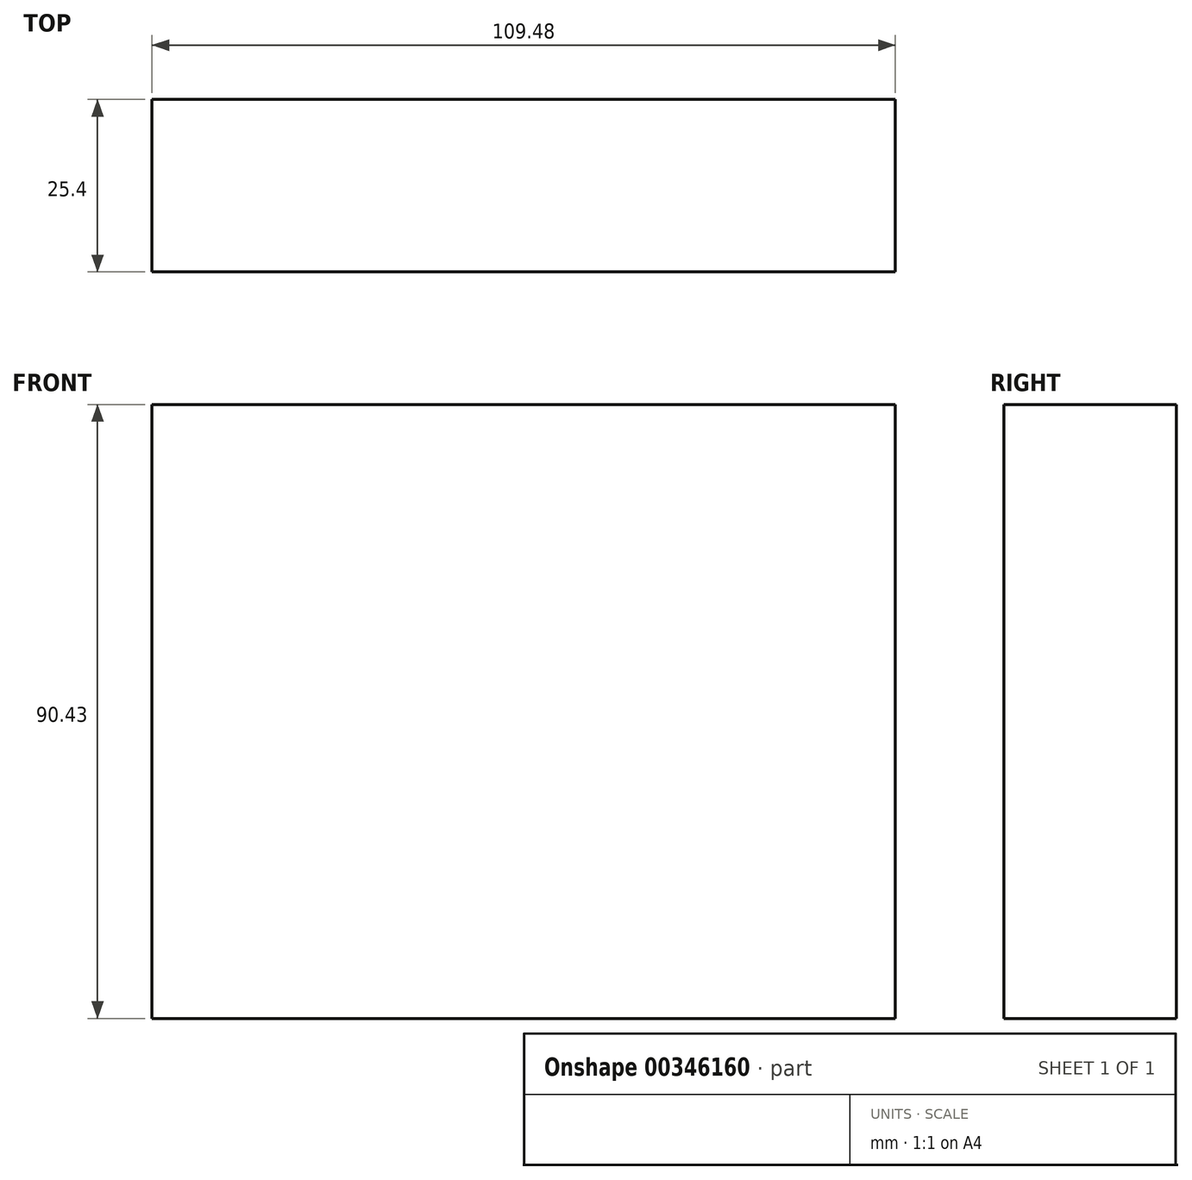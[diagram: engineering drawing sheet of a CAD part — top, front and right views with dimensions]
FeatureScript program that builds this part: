
annotation { "Feature Type Name" : "Feature", "Feature Type Description" : "" }
export const myFeature = defineFeature(function(context is Context, id is Id, definition is map)
    precondition{}
    {
        {
            var Q0;
            Q0=qCreatedBy(makeId("Front.planeOp"),FACE);
            var sketch = newSketch(context, id + "F0", { "sketchPlane" : qUnion([Q0])});
            skLineSegment(sketch, "E0", {"start": v(-49.86, 38.8) * mm, "end": v(-49.86, -51.62) * mm});
            skLineSegment(sketch, "E1", {"start": v(-49.86, -51.62) * mm, "end": v(59.62, -51.62) * mm});
            skLineSegment(sketch, "E2", {"start": v(59.62, -51.62) * mm, "end": v(59.62, 38.8) * mm});
            skLineSegment(sketch, "E3", {"start": v(59.62, 38.8) * mm, "end": v(-49.86, 38.8) * mm});
            skSolve(sketch);
        }
        {
            var Q0;
            Q0 = qSketchRegion(id + "F0", true);
            extrude(context, id + "F1", {"entities" : qUnion([Q0]), "depth" : 25.4 * mm});
        }
    });
